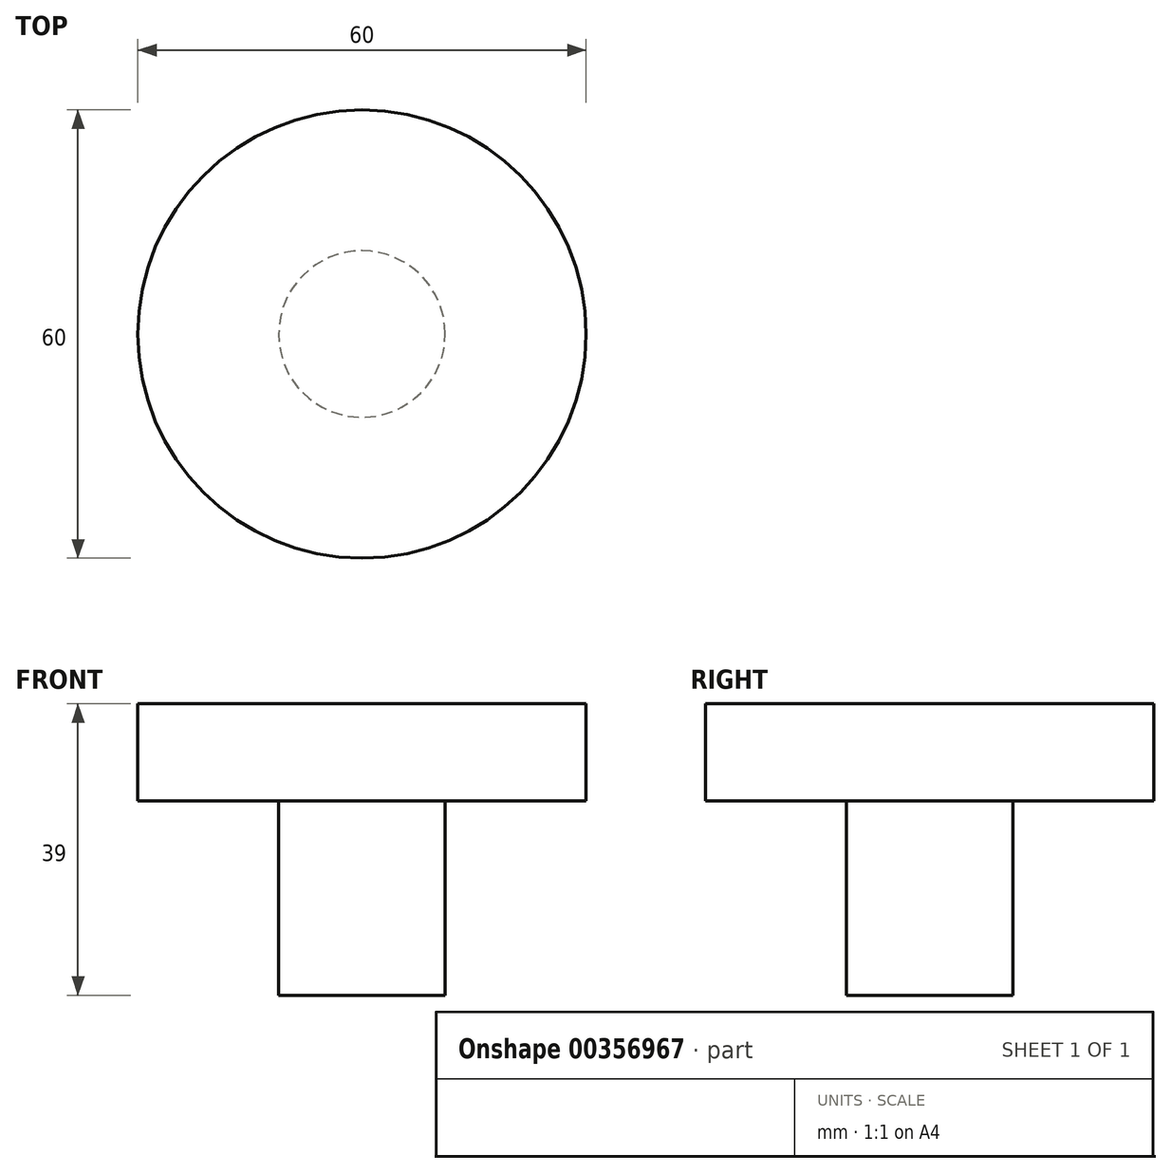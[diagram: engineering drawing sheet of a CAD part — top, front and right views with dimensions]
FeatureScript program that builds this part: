
annotation { "Feature Type Name" : "Feature", "Feature Type Description" : "" }
export const myFeature = defineFeature(function(context is Context, id is Id, definition is map)
    precondition{}
    {
        {
            var Q0;
            Q0=qCreatedBy(makeId("Front.planeOp"),FACE);
            var sketch = newSketch(context, id + "F0", { "sketchPlane" : qUnion([Q0])});
            skLineSegment(sketch, "E0", {"start": v(0, 0) * mm, "end": v(0, 39) * mm});
            skLineSegment(sketch, "E1", {"start": v(0, 39) * mm, "end": v(30, 39) * mm});
            skLineSegment(sketch, "E2", {"start": v(30, 39) * mm, "end": v(30, 26) * mm});
            skLineSegment(sketch, "E3", {"start": v(30, 26) * mm, "end": v(11.14, 26) * mm});
            skLineSegment(sketch, "E4", {"start": v(11.14, 26) * mm, "end": v(11.14, 0) * mm});
            skLineSegment(sketch, "E5", {"start": v(11.14, 0) * mm, "end": v(0, 0) * mm});
            skSolve(sketch);
        }
        {
            var Q0;
            Q0=makeQuery(id+"F0.imprint","IMPRINT",FACE,{"disambiguationData":[TD([[makeQuery(id+"F0.imprint","IMPRINT",EDGE,{"derivedFrom":sQuery(id+"F0.wireOp",EDGE,"E0")}),-1.0]])]});
            var Q1;
            Q1=sQuery(id+"F0.wireOp",EDGE,"E0");
            revolve(context, id + "F1", {"entities" : qUnion([Q0]), "axis" : qUnion([Q1]), "revolveType" : RevolveType.FULL});
        }
    });
